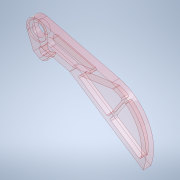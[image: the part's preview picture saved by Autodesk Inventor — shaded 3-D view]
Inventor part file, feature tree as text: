
AUTODESK INVENTOR PART (.ipt)
format: ipt  version: 2020.2 (Build 242310000, 310)  size: 563,712 bytes
history: native  units: mm
features: sketch x14, extrude x11, projected_geometry x8, other x6, fillet x5, hole x1
ambient origin geometry x8: Origin, YZ Plane, XZ Plane, XY Plane, X Axis, Y Axis, Z Axis, Center Point
bodies: Body1 (feature_tree)
feature tree (45):
  other  "ソリッド1"
  sketch  "スケッチ1"
  extrude  "押し出し1"  Depth=5.0mm TaperAngle=0.0deg
  hole  "穴1"  [1 undecoded]
  extrude  "押し出し2"  Depth=4.0mm
  sketch  "スケッチ3"
  sketch  "スケッチ4"
  extrude  "押し出し3"  Depth=3.0mm
  extrude  "押し出し4"  TaperAngle=30.0deg  [1 undecoded]
  sketch  "スケッチ5"
  extrude  "押し出し5"  Depth=2.0mm
  sketch  "スケッチ6"
  fillet  "フィレット1"  Radius=3.0mm
  sketch  "スケッチ7"
  extrude  "押し出し6"  Depth=33.664519mm
  sketch  "スケッチ9"
  extrude  "押し出し7"  Depth=3.0mm
  extrude  "押し出し8"  Depth=2.0mm
  fillet  "フィレット2"  Radius=2.0mm
  fillet  "フィレット3"  Radius=5.0mm
  fillet  "フィレット4"  Radius=14.0mm
  extrude  "押し出し9"  Depth=18.121364mm
  extrude  "押し出し10"  Depth=12.602268mm
  fillet  "フィレット5"  Radius=2.413401mm
  extrude  "押し出し11"  Depth=15.0mm
  sketch  "スケッチ2"
  projected_geometry  "投影ループ1"
  projected_geometry  "投影ループ2"
  projected_geometry  "投影ループ3"
  projected_geometry  "投影ループ4"
  projected_geometry  "投影ループ5"
  projected_geometry  "投影ループ6"
  sketch  "スケッチ8"
  projected_geometry  "投影ループ7"
  sketch  "スケッチ10"
  sketch  "スケッチ11"
  projected_geometry  "投影ループ8"
  sketch  "スケッチ12"
  sketch  "スケッチ13"
  sketch  "スケッチ14"
  other  "断面エッジを投影1"
  other  "断面エッジを投影2"
  other  "断面エッジを投影3"
  other  "断面エッジを投影4"
  other  "断面エッジを投影5"
note: 2 required parameter values undecoded (feature->parameter linkage not recoverable at this tier; creation-order binding heuristic only, values carry confidence <= 0.55)
